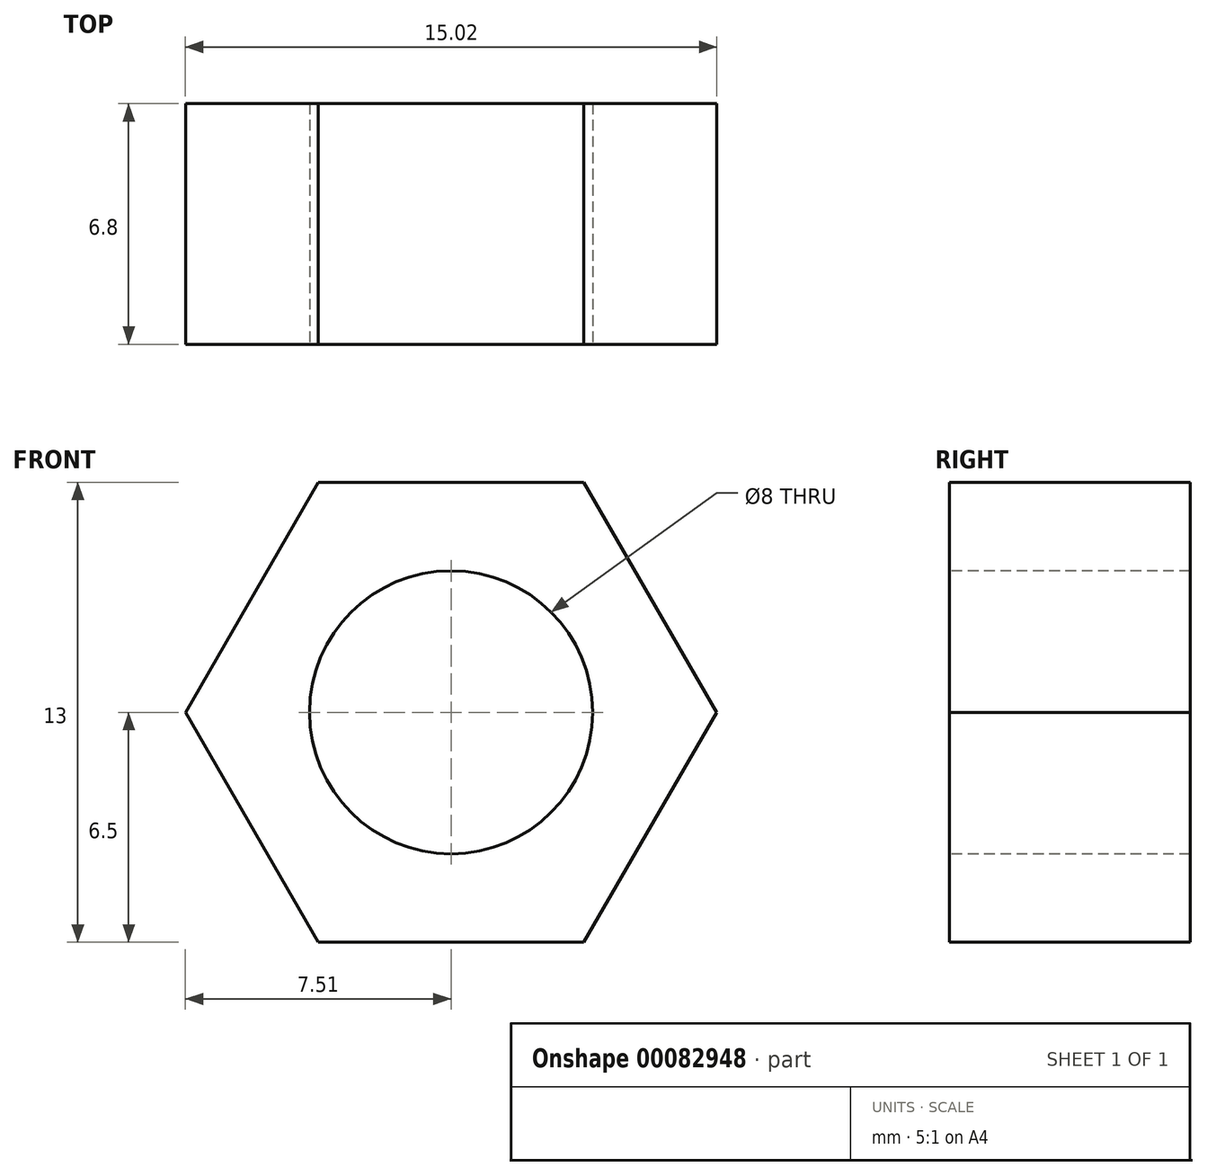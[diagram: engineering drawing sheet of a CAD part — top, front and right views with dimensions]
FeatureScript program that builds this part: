
annotation { "Feature Type Name" : "Feature", "Feature Type Description" : "" }
export const myFeature = defineFeature(function(context is Context, id is Id, definition is map)
    precondition{}
    {
        {
            var Q0;
            Q0=qCreatedBy(makeId("Front.planeOp"),FACE);
            var sketch = newSketch(context, id + "F0", { "sketchPlane" : qUnion([Q0])});
            skCircle(sketch, "E0.cCircle", {"center": v(0, 0) * mm, "radius": 7.5 * mm, "construction": true});
            skLineSegment(sketch, "E0.0", {"start": v(7.5, 0) * mm, "end": v(3.75, -6.5) * mm});
            skLineSegment(sketch, "E0.1", {"start": v(3.75, -6.5) * mm, "end": v(-3.75, -6.5) * mm});
            skLineSegment(sketch, "E0.2", {"start": v(-3.75, -6.5) * mm, "end": v(-7.5, 0) * mm});
            skLineSegment(sketch, "E0.3", {"start": v(-7.5, 0) * mm, "end": v(-3.75, 6.5) * mm});
            skLineSegment(sketch, "E0.4", {"start": v(-3.75, 6.5) * mm, "end": v(3.75, 6.5) * mm});
            skLineSegment(sketch, "E0.5", {"start": v(3.75, 6.5) * mm, "end": v(7.5, 0) * mm});
            skSolve(sketch);
        }
        {
            var Q0;
            Q0=makeQuery(id+"F0.imprint","IMPRINT",FACE,{"disambiguationData":[TD([[makeQuery(id+"F0.imprint","IMPRINT",EDGE,{"derivedFrom":sQuery(id+"F0.wireOp",EDGE,"E0.0")}),-1.0]])]});
            extrude(context, id + "F1", {"entities" : qUnion([Q0]), "depth" : 6.8 * mm});
        }
        {
            var Q0;
            Q0=makeQuery(id+"F1.opExtrude","CAP_FACE",FACE,{"disambiguationData":[OSD([sQuery(id+"F0.wireOp",EDGE,"E0.0"),sQuery(id+"F0.wireOp",EDGE,"E0.1"),sQuery(id+"F0.wireOp",EDGE,"E0.2"),sQuery(id+"F0.wireOp",EDGE,"E0.3"),sQuery(id+"F0.wireOp",EDGE,"E0.4"),sQuery(id+"F0.wireOp",EDGE,"E0.5")])],"isStart":false});
            var sketch = newSketch(context, id + "F2", { "sketchPlane" : qUnion([Q0])});
            skCircle(sketch, "E1", {"center": v(0, 0) * mm, "radius": 4 * mm});
            skSolve(sketch);
        }
        {
            var Q0;
            Q0 = qSketchRegion(id + "F2", true);
            extrude(context, id + "F3", {"entities" : qUnion([Q0]), "operationType" : NewBodyOperationType.REMOVE, "endBound" : BoundingType.THROUGH_ALL, "oppositeDirection" : true, "depth" : 25 * mm});
        }
    });
